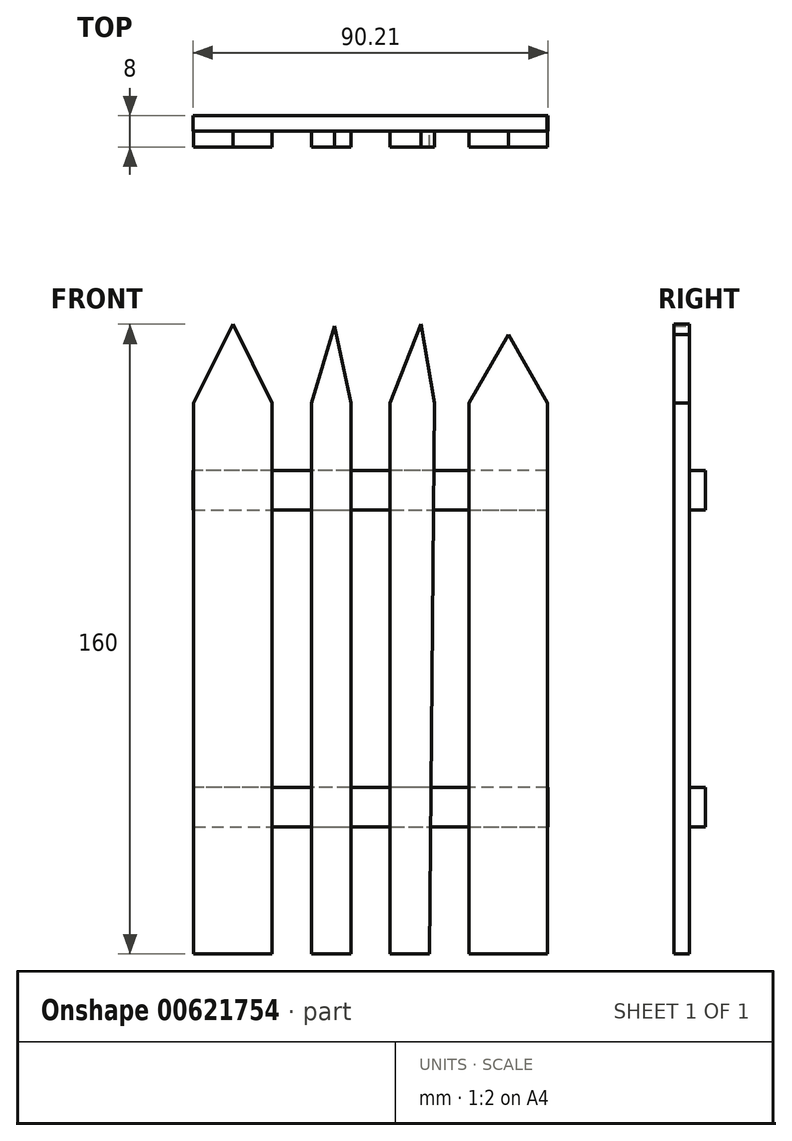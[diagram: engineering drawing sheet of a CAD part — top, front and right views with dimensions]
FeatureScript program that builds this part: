
annotation { "Feature Type Name" : "Feature", "Feature Type Description" : "" }
export const myFeature = defineFeature(function(context is Context, id is Id, definition is map)
    precondition{}
    {
        {
            var Q0;
            Q0=qCreatedBy(makeId("Front.planeOp"),FACE);
            var sketch = newSketch(context, id + "F0", { "sketchPlane" : qUnion([Q0])});
            skLineSegment(sketch, "E0", {"start": v(-61.22, 59.65) * mm, "end": v(-61.22, -80.35) * mm});
            skLineSegment(sketch, "E1", {"start": v(-61.22, -80.35) * mm, "end": v(-41.22, -80.35) * mm});
            skLineSegment(sketch, "E2", {"start": v(-41.22, -80.35) * mm, "end": v(-41.22, 59.65) * mm});
            skLineSegment(sketch, "E3", {"start": v(-41.22, 59.65) * mm, "end": v(-51.18, 79.65) * mm});
            skLineSegment(sketch, "E4", {"start": v(-51.18, 79.65) * mm, "end": v(-61.22, 59.65) * mm});
            skLineSegment(sketch, "E5", {"start": v(-41.22, 59.65) * mm, "end": v(-61.22, 59.65) * mm});
            skLineSegment(sketch, "E6", {"start": v(-51.18, 79.65) * mm, "end": v(-51.18, 59.65) * mm});
            skLineSegment(sketch, "E7", {"start": v(-41.22, -80.35) * mm, "end": v(-31.22, -80.35) * mm});
            skLineSegment(sketch, "E8", {"start": v(-31.22, -80.35) * mm, "end": v(-21.22, -80.35) * mm});
            skLineSegment(sketch, "E9", {"start": v(-21.22, -80.35) * mm, "end": v(-11.22, -80.35) * mm});
            skLineSegment(sketch, "E10", {"start": v(-11.22, -80.35) * mm, "end": v(-1.22, -80.35) * mm});
            skLineSegment(sketch, "E11", {"start": v(-1.22, -80.35) * mm, "end": v(8.78, -80.35) * mm});
            skLineSegment(sketch, "E12", {"start": v(8.78, -80.35) * mm, "end": v(28.78, -80.35) * mm});
            skLineSegment(sketch, "E13", {"start": v(28.78, -80.35) * mm, "end": v(28.78, 59.65) * mm});
            skLineSegment(sketch, "E14", {"start": v(28.78, 59.65) * mm, "end": v(18.78, 76.97) * mm});
            skLineSegment(sketch, "E15", {"start": v(18.78, 76.97) * mm, "end": v(8.78, 59.65) * mm});
            skLineSegment(sketch, "E16", {"start": v(8.78, 59.65) * mm, "end": v(8.78, -80.35) * mm});
            skLineSegment(sketch, "E17", {"start": v(28.78, 59.65) * mm, "end": v(8.78, 59.65) * mm});
            skLineSegment(sketch, "E18", {"start": v(18.78, 76.97) * mm, "end": v(18.78, 59.65) * mm});
            skLineSegment(sketch, "E19", {"start": v(-31.22, -80.35) * mm, "end": v(-31.22, 59.65) * mm});
            skLineSegment(sketch, "E20", {"start": v(-31.22, 59.65) * mm, "end": v(-25.41, 79.2) * mm});
            skLineSegment(sketch, "E21", {"start": v(-25.41, 79.2) * mm, "end": v(-21.22, 59.65) * mm});
            skLineSegment(sketch, "E22", {"start": v(-21.22, 59.65) * mm, "end": v(-21.22, -80.35) * mm});
            skLineSegment(sketch, "E23", {"start": v(-31.22, 59.65) * mm, "end": v(-21.22, 59.65) * mm});
            skLineSegment(sketch, "E24", {"start": v(-25.41, 79.2) * mm, "end": v(-26.22, 59.22) * mm});
            skPoint(sketch, "E24.endSnap0", {"position": v(-26.22, 59.65) * mm});
            skLineSegment(sketch, "E25", {"start": v(-11.22, -80.35) * mm, "end": v(-11.22, 59.64) * mm});
            skLineSegment(sketch, "E26", {"start": v(-11.22, 59.64) * mm, "end": v(-3.4, 79.64) * mm});
            skLineSegment(sketch, "E27", {"start": v(-3.4, 79.64) * mm, "end": v(0, 59.64) * mm});
            skLineSegment(sketch, "E28", {"start": v(0, 59.64) * mm, "end": v(-1.22, -80.35) * mm});
            skLineSegment(sketch, "E29", {"start": v(0, 59.64) * mm, "end": v(-11.22, 59.64) * mm});
            skLineSegment(sketch, "E30", {"start": v(-5.6, 59.64) * mm, "end": v(-3.4, 79.64) * mm});
            skLineSegment(sketch, "E31", {"start": v(-171.26, 33.93) * mm, "end": v(-193, -47.08) * mm});
            skLineSegment(sketch, "E32", {"start": v(-193, -47.08) * mm, "end": v(-228.56, 20.89) * mm});
            skLineSegment(sketch, "E33", {"start": v(-228.56, 20.89) * mm, "end": v(-197.34, -23.76) * mm});
            skLineSegment(sketch, "E34", {"start": v(-197.34, -23.76) * mm, "end": v(-176.8, 29.19) * mm});
            skLineSegment(sketch, "E35", {"start": v(-176.8, 29.19) * mm, "end": v(-198.53, -14.68) * mm});
            skLineSegment(sketch, "E36", {"start": v(-198.53, -14.68) * mm, "end": v(-228.56, 28.79) * mm});
            skLineSegment(sketch, "E37", {"start": v(-228.56, 28.79) * mm, "end": v(-200.1, -6.77) * mm});
            skLineSegment(sketch, "E38", {"start": v(-200.1, -6.77) * mm, "end": v(-182.33, 29.98) * mm});
            skLineSegment(sketch, "E39", {"start": v(-182.33, 29.98) * mm, "end": v(-200.9, 0) * mm});
            skLineSegment(sketch, "E40", {"start": v(-200.9, 0) * mm, "end": v(-222.5, 31.26) * mm});
            skLineSegment(sketch, "E41", {"start": v(-222.5, 31.26) * mm, "end": v(-200.5, 9.43) * mm});
            skLineSegment(sketch, "E42", {"start": v(-200.5, 9.43) * mm, "end": v(-187.84, 29.87) * mm});
            skLineSegment(sketch, "E43", {"start": v(-187.84, 29.87) * mm, "end": v(-201.99, 20.1) * mm});
            skLineSegment(sketch, "E44", {"start": v(-201.99, 20.1) * mm, "end": v(-213.94, 31.16) * mm});
            skLineSegment(sketch, "E45", {"start": v(-213.94, 31.16) * mm, "end": v(-201.47, 23.43) * mm});
            skLineSegment(sketch, "E46", {"start": v(-201.47, 23.43) * mm, "end": v(-193.56, 28.9) * mm});
            skLineSegment(sketch, "E47", {"start": v(-193.56, 28.9) * mm, "end": v(-201.69, 28.9) * mm});
            skLineSegment(sketch, "E48", {"start": v(-201.69, 28.9) * mm, "end": v(-210.29, 28.9) * mm});
            skLineSegment(sketch, "E49", {"start": v(-210.29, 28.9) * mm, "end": v(-171.26, 33.93) * mm});
            skSolve(sketch);
        }
        {
            var Q0;
            Q0=makeQuery(id+"F0.imprint","IMPRINT",FACE,{"disambiguationData":[TD([[makeQuery(id+"F0.imprint","IMPRINT",EDGE,{"derivedFrom":sQuery(id+"F0.wireOp",EDGE,"E12")}),1.0]])]});
            var Q1;
            Q1=makeQuery(id+"F0.imprint","IMPRINT",FACE,{"disambiguationData":[TD([[makeQuery(id+"F0.imprint","IMPRINT",EDGE,{"derivedFrom":sQuery(id+"F0.wireOp",EDGE,"E10")}),1.0]])]});
            var Q2;
            {var subQ3=sQuery(id+"F0.wireOp",EDGE,"E0");Q2=makeQuery(id+"F0.imprint","IMPRINT",FACE,{"disambiguationData":[TD([[makeQuery(id+"F0.imprint","IMPRINT",EDGE,{"derivedFrom":subQ3}),1.0]])]});}
            var Q3;
            Q3=makeQuery(id+"F0.imprint","IMPRINT",FACE,{"disambiguationData":[TD([[makeQuery(id+"F0.imprint","IMPRINT",EDGE,{"derivedFrom":sQuery(id+"F0.wireOp",EDGE,"E8")}),1.0]])]});
            var Q4;
            {var subQ0=sQuery(id+"F0.wireOp",EDGE,"E14");Q4=makeQuery(id+"F0.imprint","IMPRINT",FACE,{"disambiguationData":[TD([[makeQuery(id+"F0.imprint","IMPRINT",EDGE,{"derivedFrom":subQ0}),1.0]])]});}
            var Q5;
            {var subQ0=sQuery(id+"F0.wireOp",EDGE,"E15");Q5=makeQuery(id+"F0.imprint","IMPRINT",FACE,{"disambiguationData":[TD([[makeQuery(id+"F0.imprint","IMPRINT",EDGE,{"derivedFrom":subQ0}),1.0]])]});}
            var Q6;
            {var subQ0=sQuery(id+"F0.wireOp",EDGE,"E26");Q6=makeQuery(id+"F0.imprint","IMPRINT",FACE,{"disambiguationData":[TD([[makeQuery(id+"F0.imprint","IMPRINT",EDGE,{"derivedFrom":subQ0}),-1.0]])]});}
            var Q7;
            {var subQ0=sQuery(id+"F0.wireOp",EDGE,"E20");Q7=makeQuery(id+"F0.imprint","IMPRINT",FACE,{"disambiguationData":[TD([[makeQuery(id+"F0.imprint","IMPRINT",EDGE,{"derivedFrom":subQ0}),-1.0]])]});}
            var Q8;
            {var subQ0=sQuery(id+"F0.wireOp",EDGE,"E4");Q8=makeQuery(id+"F0.imprint","IMPRINT",FACE,{"disambiguationData":[TD([[makeQuery(id+"F0.imprint","IMPRINT",EDGE,{"derivedFrom":subQ0}),1.0]])]});}
            var Q9;
            {var subQ0=sQuery(id+"F0.wireOp",EDGE,"E3");Q9=makeQuery(id+"F0.imprint","IMPRINT",FACE,{"disambiguationData":[TD([[makeQuery(id+"F0.imprint","IMPRINT",EDGE,{"derivedFrom":subQ0}),1.0]])]});}
            var Q10;
            {var subQ0=sQuery(id+"F0.wireOp",EDGE,"E21");Q10=makeQuery(id+"F0.imprint","IMPRINT",FACE,{"disambiguationData":[TD([[makeQuery(id+"F0.imprint","IMPRINT",EDGE,{"derivedFrom":subQ0}),-1.0]])]});}
            var Q11;
            {var subQ0=sQuery(id+"F0.wireOp",EDGE,"E27");Q11=makeQuery(id+"F0.imprint","IMPRINT",FACE,{"disambiguationData":[TD([[makeQuery(id+"F0.imprint","IMPRINT",EDGE,{"derivedFrom":subQ0}),-1.0]])]});}
            extrude(context, id + "F1", {"entities" : qUnion([Q0, Q1, Q2, Q3, Q4, Q5, Q6, Q7, Q8, Q9, Q10, Q11]), "depth" : 4 * mm, "offsetDistance" : 25 * mm});
        }
        {
            var Q0;
            Q0=qCreatedBy(makeId("Front.planeOp"),FACE);
            var sketch = newSketch(context, id + "F2", { "sketchPlane" : qUnion([Q0])});
            skLineSegment(sketch, "E50", {"start": v(28.66, 42.5) * mm, "end": v(-61.34, 42.5) * mm});
            skLineSegment(sketch, "E51", {"start": v(-61.34, 42.5) * mm, "end": v(-61.34, 32.5) * mm});
            skLineSegment(sketch, "E52", {"start": v(-61.34, 32.5) * mm, "end": v(28.66, 32.5) * mm});
            skLineSegment(sketch, "E53", {"start": v(28.66, 32.5) * mm, "end": v(28.66, 42.5) * mm});
            skSolve(sketch);
        }
        {
            var Q0;
            Q0=makeQuery(id+"F2.imprint","IMPRINT",FACE,{"disambiguationData":[TD([[makeQuery(id+"F2.imprint","IMPRINT",EDGE,{"derivedFrom":sQuery(id+"F2.wireOp",EDGE,"E50")}),1.0]])]});
            extrude(context, id + "F3", {"entities" : qUnion([Q0]), "oppositeDirection" : true, "depth" : 4 * mm, "offsetDistance" : 25 * mm});
        }
        {
            var Q0;
            Q0=qCreatedBy(makeId("Front.planeOp"),FACE);
            var sketch = newSketch(context, id + "F4", { "sketchPlane" : qUnion([Q0])});
            skLineSegment(sketch, "E54", {"start": v(28.87, -38.03) * mm, "end": v(-61.13, -38.03) * mm});
            skLineSegment(sketch, "E55", {"start": v(-61.13, -38.03) * mm, "end": v(-61.13, -48.03) * mm});
            skLineSegment(sketch, "E56", {"start": v(-61.13, -48.03) * mm, "end": v(28.87, -48.03) * mm});
            skLineSegment(sketch, "E57", {"start": v(28.87, -48.03) * mm, "end": v(28.87, -38.03) * mm});
            skSolve(sketch);
        }
        {
            var Q0;
            Q0 = qSketchRegion(id + "F4", true);
            extrude(context, id + "F5", {"entities" : qUnion([Q0]), "oppositeDirection" : true, "depth" : 4 * mm, "offsetDistance" : 25 * mm});
        }
    });
